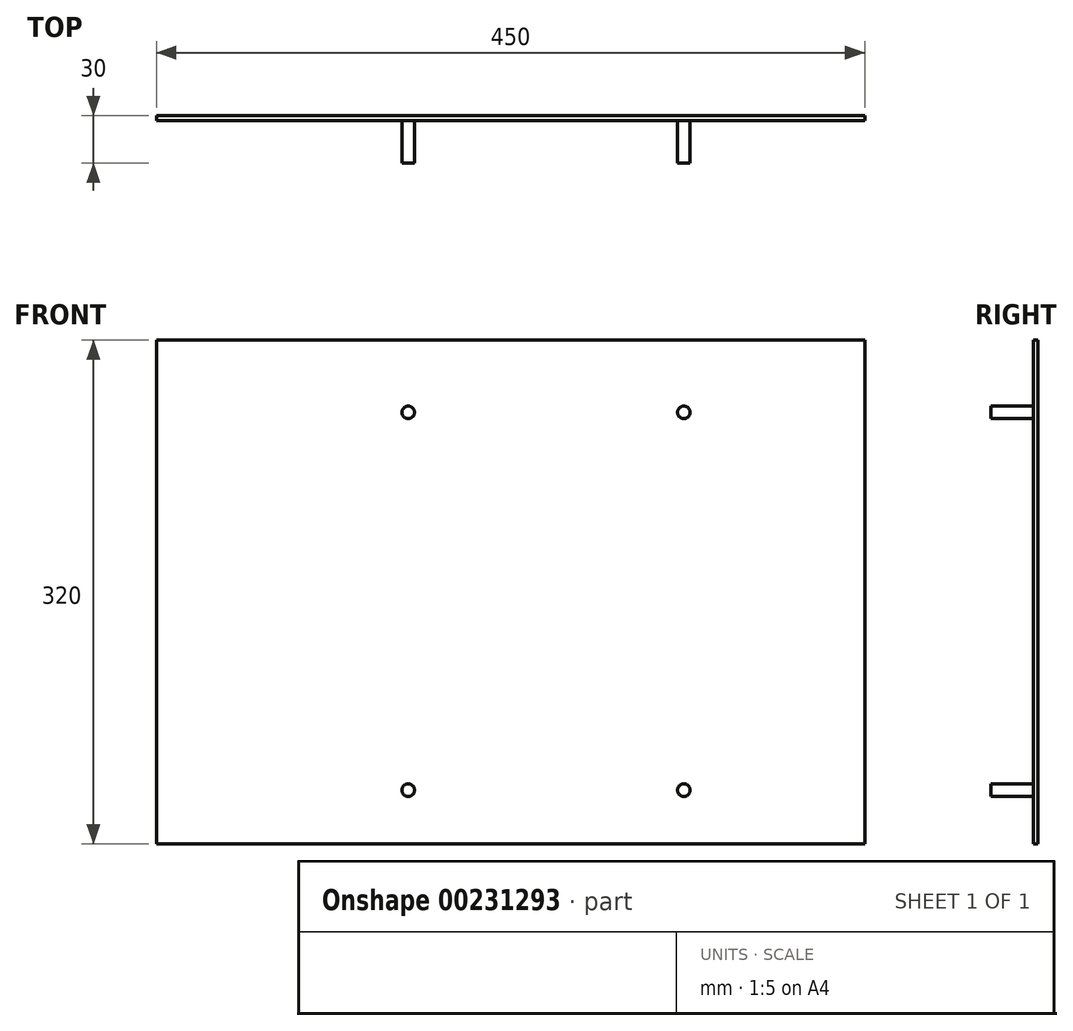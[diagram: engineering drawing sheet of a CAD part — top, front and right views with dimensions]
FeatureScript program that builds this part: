
annotation { "Feature Type Name" : "Feature", "Feature Type Description" : "" }
export const myFeature = defineFeature(function(context is Context, id is Id, definition is map)
    precondition{}
    {
        {
            var Q0;
            Q0=qCreatedBy(makeId("Front.planeOp"),FACE);
            var sketch = newSketch(context, id + "F0", { "sketchPlane" : qUnion([Q0])});
            skLineSegment(sketch, "E0.bottom", {"start": v(223, -160) * mm, "end": v(-227, -160) * mm});
            skLineSegment(sketch, "E0.top", {"start": v(223, 160) * mm, "end": v(-227, 160) * mm});
            skLineSegment(sketch, "E0.left", {"start": v(223, -160) * mm, "end": v(223, 160) * mm});
            skLineSegment(sketch, "E0.right", {"start": v(-227, -160) * mm, "end": v(-227, 160) * mm});
            skPoint(sketch, "E0.middle", {"position": v(-2, -22) * mm});
            skLineSegment(sketch, "E1.bottom", {"start": v(124.82, -150) * mm, "end": v(-85.18, -150) * mm});
            skLineSegment(sketch, "E1.top", {"start": v(124.82, 150) * mm, "end": v(-85.18, 150) * mm});
            skLineSegment(sketch, "E1.left", {"start": v(124.82, -150) * mm, "end": v(124.82, 150) * mm});
            skLineSegment(sketch, "E1.right", {"start": v(-85.18, -150) * mm, "end": v(-85.18, 150) * mm});
            skPoint(sketch, "E1.middle", {"position": v(17.82, -22) * mm});
            skCircle(sketch, "E2", {"center": v(-67, 114.09) * mm, "radius": 4 * mm});
            skCircle(sketch, "E3.0.1.0", {"center": v(-67, -125.91) * mm, "radius": 4 * mm});
            skCircle(sketch, "E3.1.0.0", {"center": v(108, 114.09) * mm, "radius": 4 * mm});
            skCircle(sketch, "E3.1.1.0", {"center": v(108, -125.91) * mm, "radius": 4 * mm});
            skLineSegment(sketch, "E3.direction1", {"start": v(-67, 114.09) * mm, "end": v(108, 114.09) * mm, "construction": true});
            skLineSegment(sketch, "E3.direction2", {"start": v(-67, 114.09) * mm, "end": v(-67, -125.91) * mm, "construction": true});
            skLineSegment(sketch, "E4", {"start": v(-227, 0) * mm, "end": v(254.47, 0) * mm, "construction": true});
            skPoint(sketch, "E4.endSnap0", {"position": v(223, 0) * mm});
            skSolve(sketch);
        }
        {
            var Q0;
            Q0=makeQuery(id+"F0.imprint","IMPRINT",FACE,{"disambiguationData":[TD([[makeQuery(id+"F0.imprint","IMPRINT",EDGE,{"derivedFrom":sQuery(id+"F0.wireOp",EDGE,"E0.bottom")}),-1.0]])]});
            var Q1;
            Q1=makeQuery(id+"F0.imprint","IMPRINT",FACE,{"disambiguationData":[TD([[makeQuery(id+"F0.imprint","IMPRINT",EDGE,{"derivedFrom":sQuery(id+"F0.wireOp",EDGE,"E1.bottom")}),-1.0]])]});
            extrude(context, id + "F1", {"entities" : qUnion([Q0, Q1]), "depth" : 3 * mm});
        }
        {
            var Q0;
            Q0=makeQuery(id+"F0.imprint","IMPRINT",FACE,{"disambiguationData":[TD([[makeQuery(id+"F0.imprint","IMPRINT",EDGE,{"derivedFrom":sQuery(id+"F0.wireOp",EDGE,"E2")}),1.0]])]});
            var Q1;
            Q1=makeQuery(id+"F0.imprint","IMPRINT",FACE,{"disambiguationData":[TD([[makeQuery(id+"F0.imprint","IMPRINT",EDGE,{"derivedFrom":sQuery(id+"F0.wireOp",EDGE,"E3.1.0.0")}),1.0]])]});
            var Q2;
            Q2=makeQuery(id+"F0.imprint","IMPRINT",FACE,{"disambiguationData":[TD([[makeQuery(id+"F0.imprint","IMPRINT",EDGE,{"derivedFrom":sQuery(id+"F0.wireOp",EDGE,"E3.0.1.0")}),1.0]])]});
            var Q3;
            Q3=makeQuery(id+"F0.imprint","IMPRINT",FACE,{"disambiguationData":[TD([[makeQuery(id+"F0.imprint","IMPRINT",EDGE,{"derivedFrom":sQuery(id+"F0.wireOp",EDGE,"E3.1.1.0")}),1.0]])]});
            extrude(context, id + "F2", {"entities" : qUnion([Q0, Q1, Q2, Q3]), "operationType" : NewBodyOperationType.ADD, "depth" : 30 * mm});
        }
    });
